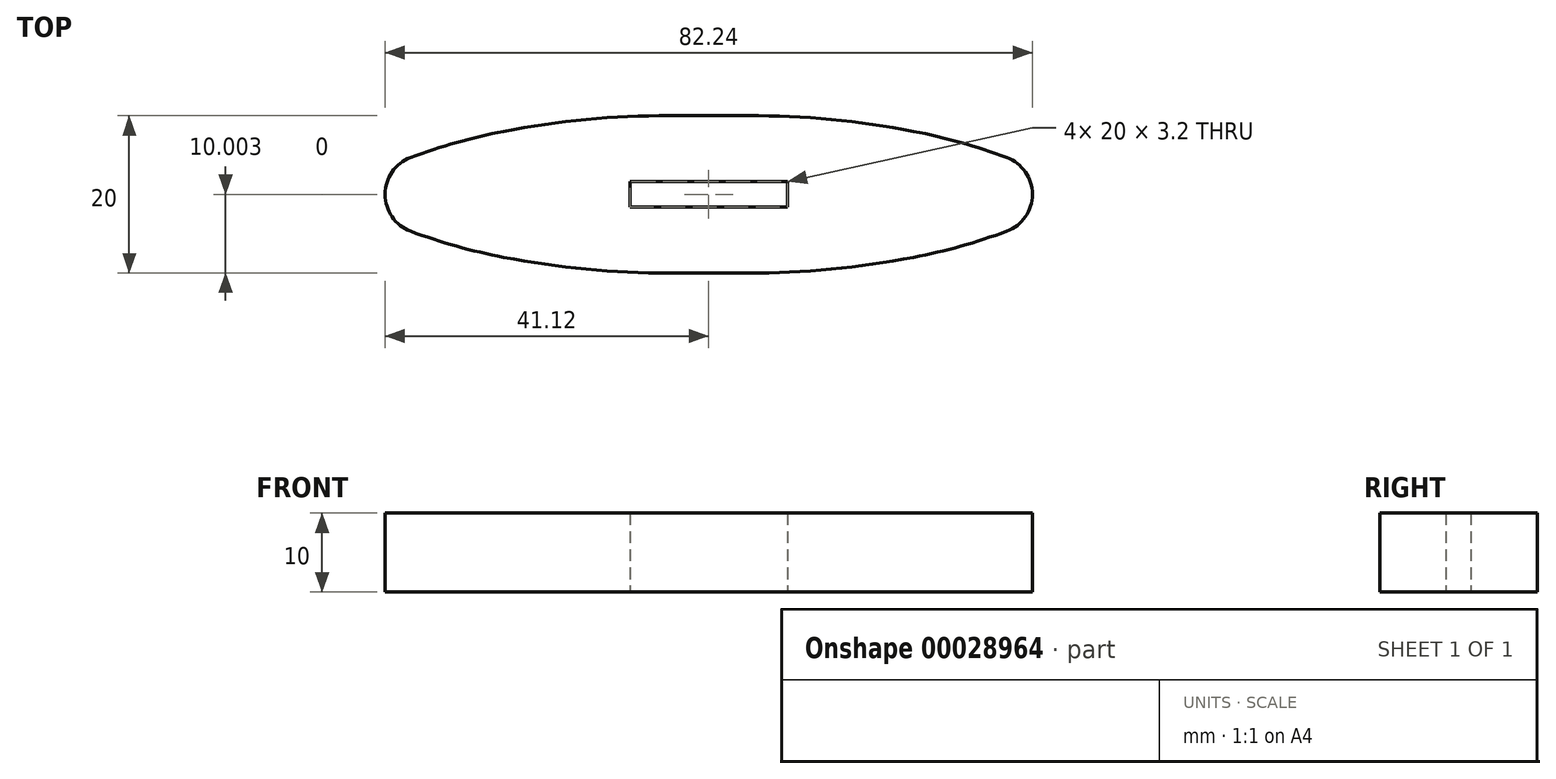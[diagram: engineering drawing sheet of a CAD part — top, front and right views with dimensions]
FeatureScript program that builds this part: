
annotation { "Feature Type Name" : "Feature", "Feature Type Description" : "" }
export const myFeature = defineFeature(function(context is Context, id is Id, definition is map)
    precondition{}
    {
        {
            var Q0;
            Q0=qCreatedBy(makeId("Top.planeOp"),FACE);
            var sketch = newSketch(context, id + "F0", { "sketchPlane" : qUnion([Q0])});
            skLineSegment(sketch, "E0", {"start": v(0, 0) * mm, "end": v(0, 63.05) * mm, "construction": true});
            skPoint(sketch, "E1", {"position": v(0, 31.52) * mm});
            skLineSegment(sketch, "E2.bottom", {"start": v(0, 31.52) * mm, "end": v(-10, 31.52) * mm});
            skLineSegment(sketch, "E2.top", {"start": v(0, 34.72) * mm, "end": v(-10, 34.72) * mm});
            skLineSegment(sketch, "E2.left", {"start": v(0, 31.52) * mm, "end": v(0, 34.72) * mm});
            skLineSegment(sketch, "E2.right", {"start": v(-10, 31.52) * mm, "end": v(-10, 34.72) * mm});
            skPoint(sketch, "E3", {"position": v(0, 33.12) * mm});
            skPoint(sketch, "E4", {"position": v(-48, 33.12) * mm});
            skLineSegment(sketch, "E5", {"start": v(0, 33.12) * mm, "end": v(-68.68, 33.12) * mm, "construction": true});
            skPoint(sketch, "E6", {"position": v(0, 43.12) * mm});
            skPoint(sketch, "E7", {"position": v(-26.03, 41.12) * mm});
            skPoint(sketch, "E8", {"position": v(-5, 43.12) * mm});
            skLineSegment(sketch, "E9", {"start": v(0, 43.12) * mm, "end": v(-5, 43.12) * mm});
            skArc(sketch, "E10", {"start": v(-5, 43.12) * mm, "mid": v(-15.56, 42.62) * mm, "end": v(-26.03, 41.12) * mm});
            skArc(sketch, "E11", {"start": v(-26.03, 41.12) * mm, "mid": v(-37.34, 38) * mm, "end": v(-48, 33.12) * mm});
            skArc(sketch, "E12.MirrorCS", {"start": v(-26.03, 25.12) * mm, "mid": v(-37.34, 28.24) * mm, "end": v(-48, 33.12) * mm});
            skArc(sketch, "E13.MirrorCS", {"start": v(-5, 23.12) * mm, "mid": v(-15.56, 23.62) * mm, "end": v(-26.03, 25.12) * mm});
            skLineSegment(sketch, "E14.MirrorCS", {"start": v(0, 23.12) * mm, "end": v(-5, 23.12) * mm});
            skLineSegment(sketch, "E15.MirrorCS", {"start": v(0, 43.12) * mm, "end": v(5, 43.12) * mm});
            skLineSegment(sketch, "E16.MirrorCS", {"start": v(0, 23.12) * mm, "end": v(5, 23.12) * mm});
            skArc(sketch, "E17.MirrorCS", {"start": v(5, 23.12) * mm, "mid": v(15.56, 23.62) * mm, "end": v(26.03, 25.12) * mm});
            skArc(sketch, "E18.MirrorCS", {"start": v(26.03, 25.12) * mm, "mid": v(37.34, 28.24) * mm, "end": v(48, 33.12) * mm});
            skArc(sketch, "E19.MirrorCS", {"start": v(26.03, 41.12) * mm, "mid": v(37.34, 38) * mm, "end": v(48, 33.12) * mm});
            skArc(sketch, "E20.MirrorCS", {"start": v(5, 43.12) * mm, "mid": v(15.56, 42.62) * mm, "end": v(26.03, 41.12) * mm});
            skLineSegment(sketch, "E21.MirrorCS", {"start": v(0, 34.72) * mm, "end": v(10, 34.72) * mm});
            skLineSegment(sketch, "E22.MirrorCS", {"start": v(10, 31.52) * mm, "end": v(10, 34.72) * mm});
            skLineSegment(sketch, "E23.MirrorCS", {"start": v(0, 31.52) * mm, "end": v(10, 31.52) * mm});
            skSolve(sketch);
        }
        {
            var Q0;
            Q0=makeQuery(id+"F0.imprint","IMPRINT",FACE,{"disambiguationData":[TD([[makeQuery(id+"F0.imprint","IMPRINT",EDGE,{"derivedFrom":sQuery(id+"F0.wireOp",EDGE,"E2.bottom")}),1.0]])]});
            extrude(context, id + "F1", {"entities" : qUnion([Q0]), "depth" : 10 * mm});
        }
        {
            var Q0;
            Q0=makeQuery(id+"F1.opExtrude","SWEPT_EDGE",EDGE,{"disambiguationData":[OSD([sQuery(id+"F0.wireOp",EDGE,"E11"),sQuery(id+"F0.wireOp",EDGE,"E12.MirrorCS")])]});
            var Q1;
            Q1=makeQuery(id+"F1.opExtrude","SWEPT_EDGE",EDGE,{"disambiguationData":[OSD([sQuery(id+"F0.wireOp",EDGE,"E18.MirrorCS"),sQuery(id+"F0.wireOp",EDGE,"E19.MirrorCS")])]});
            fillet(context, id + "F2", {"entities" : qUnion([Q0, Q1]), "radius" : 5 * mm, "tangentPropagation" : true, "allowEdgeOverflow" : false});
        }
    });
